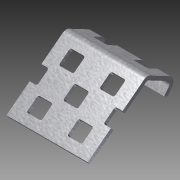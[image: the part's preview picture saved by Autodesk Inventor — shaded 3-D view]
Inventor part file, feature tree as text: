
AUTODESK INVENTOR PART (.ipt)
format: ipt  version: 2012 (Build 160160000, 160)  size: 1,103,872 bytes
history: native  units: in
note: dims shown in document units (in); Inventor stores cm internally (conversion verified against a paired STEP export)
features: sketch x7, other x3, plane x2, split x2, imported_body x1, fillet x1
ambient origin geometry x8: Origin, YZ Plane, XZ Plane, XY Plane, X Axis, Y Axis, Z Axis, Center Point
feature tree (16):
  parser-record x1  (decoder bookkeeping rows leaked as tree rows — omitted from the tree; the rows remain in map.json)
  imported_body  "Base1"
  sketch  "Sketch1"  dims[d0=6.2992in d2=0.5in d3=0.3937in d5=1.0in]
  sketch  "Sketch2"  dims[d7=6.2992in d9=0.5in d10=0.7874in d12=0.5in]
  sketch  "Sketch3"  dims[d15=5.9055in d17=0.5in d18=0.3937in d20=1.0in d22=0.1in d23=0.1718in]
  sketch  "Sketch4"  dims[d24=0.04in d25=0.6871in]
  plane  "Work Plane1"
  split  "Split1"
  plane  "Work Plane2"
  split  "Split2"
  sketch  "Sketch5"  dims[d26=0.025in]
  sketch  "Sketch6"
  other  "Bend Part1"
  other  "Bend Part2"
  fillet  "Fillet1"  Radius=0.1in
  sketch  "Sketch7"
